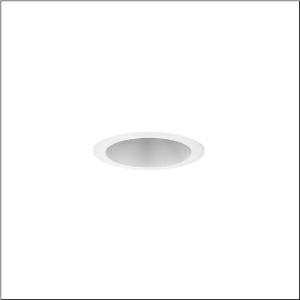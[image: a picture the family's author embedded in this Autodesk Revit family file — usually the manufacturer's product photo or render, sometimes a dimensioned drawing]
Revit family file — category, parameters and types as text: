
# Revit family: lunis_31_mini_51dn157e31
name_source: partatom
category: Lighting Fixtures
units: mm (PartAtom-declared; Revit-internal decimal feet)

## family parameters
Cut with Voids When Loaded = No
Host = Face
Light Source = No
Part Type = Normal
Room Calculation Point = No
Round Connector Dimension = Use Diameter
Shared = No

## types (1)
- Lunis 31 mini (1 x LED, 1000 lm, 8.3 W, 3000K)
    Apparent Load = 8 VA
    CIE Flux Codes = 93 98 100 100 100
    Color Rendering = 80
    Color Temperature = 3000K
    Default Elevation = 1800 mm
    Description = Lunis 31,  mini, downlight, light control with lens, light emission: direct distribution, LED rated luminous flux: 1.000lm, light colour: 830, mains connection: 220..240V, AC, 50/60Hz, housing, white, protection rating (complete): IP20, protection rating (on room side): IP54, insulation class (complete): insulation class II (safety insulation), certification: CE, packaging unit: 1 piece
    Height = 0 mm  [stored 0 ft]
    Lamp = 1 x LED
    Lamp Light Flux = 1000 lm
    Lamp Power = 8.3 W
    Lamp count = 1
    Length = 188 mm  [stored 0.616798 ft]
    Luminous efficacy = 120 lm/W
    Manufacturer = Siteco
    ModVariant = No
    Model = 51DN157E31
    Mounting Place = Ceiling
    Mounting Type = Recessed
    Number of Poles = 1
    OnlyDefault = Yes
    Power Factor = 1
    Product Name = Lunis 31 mini
    Product group = downlight
    ProductGroupID = 400
    Protection Class = Protection class II
    Protection Degree = IP 20
    RLX_Detail_Level = 1
    RLX_Emergency_Light_Flux = 0 lm
    RLX_Emergency_Type = 0
    RLX_Emergency_Type_DB = No
    RlxData = <blob elided: 21789 chars, md5=db9c80a4>
    Socket = socket
    Standby Power = 0 W
    System Light Flux = 1000 lm
    System Power = 8 W
    Type Comments = Product without accessories
    Type Image = l_1005624.jpg
    URL = http://relux.com
    VarID = ---
    Voltage = 0 V
    Weight = 0.00 kg
    Width = 0 mm  [stored 0 ft]

note: [stored X ft] marks values corroborated as IEEE doubles in the binary element streams (Revit-internal decimal feet)

## geometry (parser evidence)
native form markers: Blend x4, Sweep x14
no freeform markers — native parametric forms only
